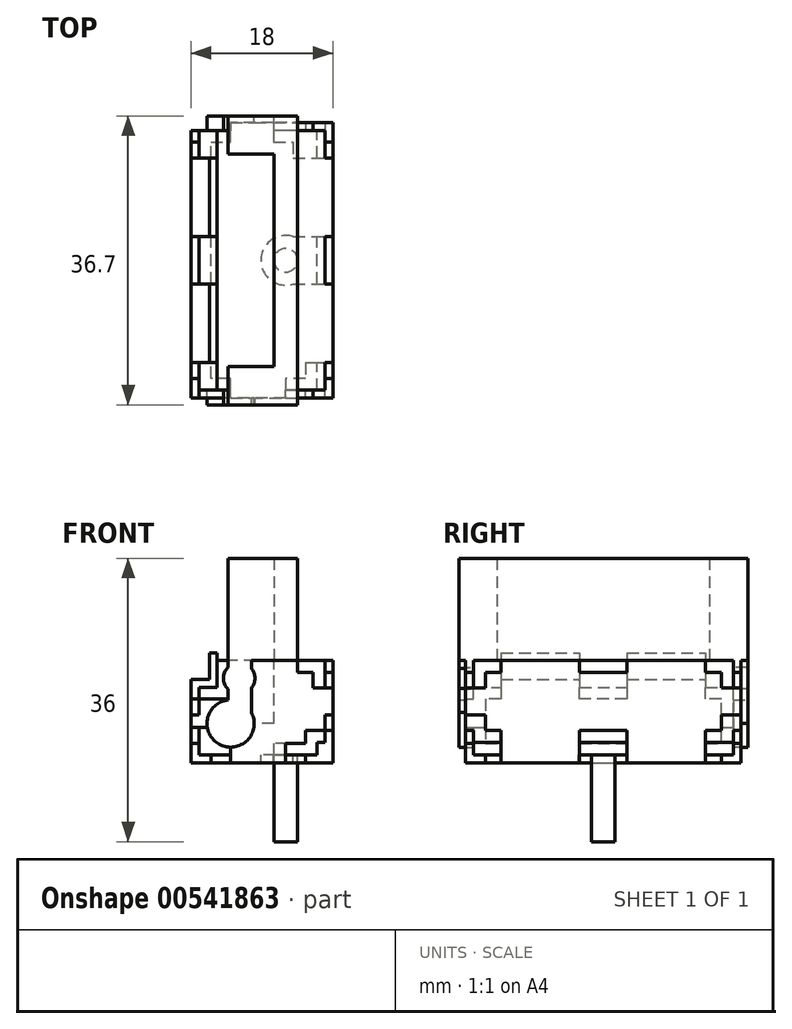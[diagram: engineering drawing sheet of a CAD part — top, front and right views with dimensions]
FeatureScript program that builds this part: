
annotation { "Feature Type Name" : "Feature", "Feature Type Description" : "" }
export const myFeature = defineFeature(function(context is Context, id is Id, definition is map)
    precondition{}
    {
        {
            var Q0;
            Q0=qCreatedBy(makeId("Front.planeOp"),FACE);
            var sketch = newSketch(context, id + "F0", { "sketchPlane" : qUnion([Q0])});
            skLineSegment(sketch, "E0", {"start": v(0, 0) * mm, "end": v(0, 8.6) * mm});
            skLineSegment(sketch, "E1", {"start": v(0, 8.6) * mm, "end": v(2.3, 8.6) * mm});
            skLineSegment(sketch, "E2", {"start": v(2.3, 8.6) * mm, "end": v(2.3, 12) * mm});
            skLineSegment(sketch, "E3", {"start": v(2.3, 12) * mm, "end": v(16, 12) * mm});
            skLineSegment(sketch, "E4", {"start": v(16, 12) * mm, "end": v(16, 1.6) * mm});
            skLineSegment(sketch, "E5", {"start": v(16, 1.6) * mm, "end": v(15, 1.6) * mm});
            skLineSegment(sketch, "E6", {"start": v(15, 1.6) * mm, "end": v(15, 0) * mm});
            skLineSegment(sketch, "E7", {"start": v(15, 0) * mm, "end": v(0, 0) * mm});
            skCircle(sketch, "E8", {"center": v(4, 4) * mm, "radius": 3 * mm});
            skCircle(sketch, "E9", {"center": v(5.1, 9.75) * mm, "radius": 2 * mm});
            skSolve(sketch);
        }
        {
            var Q0;
            Q0=makeQuery(id+"F0.imprint","IMPRINT",FACE,{"disambiguationData":[TD([[makeQuery(id+"F0.imprint","IMPRINT",EDGE,{"derivedFrom":sQuery(id+"F0.wireOp",EDGE,"E8")}),1.0]])]});
            var Q1;
            Q1=makeQuery(id+"F0.imprint","IMPRINT",FACE,{"disambiguationData":[TD([[makeQuery(id+"F0.imprint","IMPRINT",EDGE,{"derivedFrom":sQuery(id+"F0.wireOp",EDGE,"E9")}),1.0]])]});
            var Q2;
            Q2=makeQuery(id+"F0.imprint","IMPRINT",FACE,{"disambiguationData":[TD([[makeQuery(id+"F0.imprint","IMPRINT",EDGE,{"derivedFrom":sQuery(id+"F0.wireOp",EDGE,"E0")}),-1.0]])]});
            extrude(context, id + "F1", {"entities" : qUnion([Q0, Q1, Q2]), "depth" : 16.5 * mm, "offsetDistance" : 25 * mm, "hasSecondDirection" : true, "secondDirectionOppositeDirection" : true, "secondDirectionDepth" : 16.5 * mm});
        }
        {
            var Q0;
            Q0=makeQuery(id+"F1.opExtrude","SWEPT_FACE",FACE,{"disambiguationData":[OSD([sQuery(id+"F0.wireOp",EDGE,"E7")])]});
            var sketch = newSketch(context, id + "F2", { "sketchPlane" : qUnion([Q0])});
            skCircle(sketch, "E10", {"center": v(11, 0) * mm, "radius": 2.5 * mm});
            skCircle(sketch, "E11", {"center": v(11, 0) * mm, "radius": 1.5 * mm});
            skLineSegment(sketch, "E12", {"start": v(12.5, -18.35) * mm, "end": v(12.5, 18.35) * mm});
            skLineSegment(sketch, "E13", {"start": v(9.5, -18.35) * mm, "end": v(9.5, 18.35) * mm});
            skLineSegment(sketch, "E14", {"start": v(12.5, -18.35) * mm, "end": v(9.5, -18.35) * mm});
            skLineSegment(sketch, "E15", {"start": v(9.5, 18.35) * mm, "end": v(12.5, 18.35) * mm});
            skSolve(sketch);
        }
        {
            var Q0;
            Q0=makeQuery(id+"F0.imprint","IMPRINT",FACE,{"disambiguationData":[TD([[makeQuery(id+"F0.imprint","IMPRINT",EDGE,{"derivedFrom":sQuery(id+"F0.wireOp",EDGE,"E8")}),1.0]])]});
            extrude(context, id + "F3", {"entities" : qUnion([Q0]), "operationType" : NewBodyOperationType.ADD, "depth" : 36.7 * mm, "offsetDistance" : 25 * mm, "symmetric" : true});
        }
        {
            var Q0;
            Q0=makeQuery(id+"F2.imprint","IMPRINT",FACE,{"disambiguationData":[TD([[makeQuery(id+"F2.imprint","IMPRINT",EDGE,{"derivedFrom":sQuery(id+"F2.wireOp",EDGE,"E11")}),1.0]])]});
            var Q1;
            Q1=sQuery(id+"F2.wireOp",EDGE,"E11");
            extrude(context, id + "F4", {"entities" : qUnion([Q0]), "operationType" : NewBodyOperationType.ADD, "surfaceEntities" : qUnion([Q1]), "depth" : 11 * mm, "offsetDistance" : 25 * mm});
        }
        {
            var Q0;
            Q0=makeQuery(id+"F0.imprint","IMPRINT",FACE,{"disambiguationData":[TD([[makeQuery(id+"F0.imprint","IMPRINT",EDGE,{"derivedFrom":sQuery(id+"F0.wireOp",EDGE,"E9")}),1.0]])]});
            extrude(context, id + "F5", {"entities" : qUnion([Q0]), "operationType" : NewBodyOperationType.ADD, "depth" : 18.35 * mm, "offsetDistance" : 25 * mm});
        }
        {
            var Q0;
            Q0=makeQuery(id+"F0.imprint","IMPRINT",FACE,{"disambiguationData":[TD([[makeQuery(id+"F0.imprint","IMPRINT",EDGE,{"derivedFrom":sQuery(id+"F0.wireOp",EDGE,"E9")}),1.0]])]});
            extrude(context, id + "F6", {"entities" : qUnion([Q0]), "oppositeDirection" : true, "depth" : 18.35 * mm, "offsetDistance" : 25 * mm});
        }
        {
            var Q0;
            {var subQ0=sQuery(id+"F2.wireOp",EDGE,"E15");Q0=makeQuery(id+"F2.imprint","IMPRINT",FACE,{"disambiguationData":[TD([[makeQuery(id+"F2.imprint","IMPRINT",EDGE,{"derivedFrom":subQ0}),-1.0]])]});}
            var Q1;
            {var subQ0=sQuery(id+"F2.wireOp",EDGE,"E13");var subQ1=sQuery(id+"F2.wireOp",EDGE,"E10");var subQ2=makeQuery(id+"F2.imprint","INTERSECT",VERTEX,{"disambiguationData":[OD(0.0)],"derivedFrom":[subQ1,subQ0]});Q1=makeQuery(id+"F2.imprint","IMPRINT",FACE,{"disambiguationData":[TD([[makeQuery(id+"F2.imprint","IMPRINT",EDGE,{"disambiguationData":[TD([[subQ2,1.0]])],"derivedFrom":subQ1}),-1.0]])]});}
            var Q2;
            {var subQ0=sQuery(id+"F2.wireOp",EDGE,"E13");var subQ1=sQuery(id+"F2.wireOp",EDGE,"E10");var subQ2=makeQuery(id+"F2.imprint","INTERSECT",VERTEX,{"disambiguationData":[OD(0.0)],"derivedFrom":[subQ1,subQ0]});Q2=makeQuery(id+"F2.imprint","IMPRINT",FACE,{"disambiguationData":[TD([[makeQuery(id+"F2.imprint","IMPRINT",EDGE,{"disambiguationData":[TD([[subQ2,1.0]])],"derivedFrom":subQ1}),1.0]])]});}
            var Q3;
            {var subQ0=sQuery(id+"F2.wireOp",EDGE,"E11");var subQ1=makeQuery(id+"F2.imprint","INTERSECT",VERTEX,{"derivedFrom":[subQ0,sQuery(id+"F2.wireOp",EDGE,"E12")]});Q3=makeQuery(id+"F2.imprint","IMPRINT",FACE,{"disambiguationData":[TD([[makeQuery(id+"F2.imprint","IMPRINT",EDGE,{"disambiguationData":[TD([[subQ1,-1.0]])],"derivedFrom":subQ0}),1.0]])]});}
            var Q4;
            {var subQ0=sQuery(id+"F2.wireOp",EDGE,"E13");var subQ1=sQuery(id+"F2.wireOp",EDGE,"E10");var subQ2=makeQuery(id+"F2.imprint","INTERSECT",VERTEX,{"disambiguationData":[OD(1.0)],"derivedFrom":[subQ1,subQ0]});Q4=makeQuery(id+"F2.imprint","IMPRINT",FACE,{"disambiguationData":[TD([[makeQuery(id+"F2.imprint","IMPRINT",EDGE,{"disambiguationData":[TD([[subQ2,-1.0]])],"derivedFrom":subQ1}),1.0]])]});}
            var Q5;
            {var subQ0=sQuery(id+"F2.wireOp",EDGE,"E13");var subQ1=sQuery(id+"F2.wireOp",EDGE,"E10");var subQ2=makeQuery(id+"F2.imprint","INTERSECT",VERTEX,{"disambiguationData":[OD(1.0)],"derivedFrom":[subQ1,subQ0]});Q5=makeQuery(id+"F2.imprint","IMPRINT",FACE,{"disambiguationData":[TD([[makeQuery(id+"F2.imprint","IMPRINT",EDGE,{"disambiguationData":[TD([[subQ2,-1.0]])],"derivedFrom":subQ1}),-1.0]])]});}
            var Q6;
            {var subQ0=sQuery(id+"F2.wireOp",EDGE,"E14");Q6=makeQuery(id+"F2.imprint","IMPRINT",FACE,{"disambiguationData":[TD([[makeQuery(id+"F2.imprint","IMPRINT",EDGE,{"derivedFrom":subQ0}),-1.0]])]});}
            var Q7;
            Q7=makeQuery(id+"F1.opExtrude","SWEPT_FACE",FACE,{"disambiguationData":[OSD([sQuery(id+"F0.wireOp",EDGE,"E3")])]});
            var Q8;
            Q8=makeQuery(id+"F1.opExtrude","SWEPT_FACE",FACE,{"disambiguationData":[OSD([sQuery(id+"F0.wireOp",EDGE,"E3")])]});
            extrude(context, id + "F7", {"entities" : qUnion([Q0, Q1, Q2, Q3, Q4, Q5, Q6]), "operationType" : NewBodyOperationType.ADD, "oppositeDirection" : true, "depth" : 25 * mm, "endBoundEntityFace" : qUnion([Q7]), "offsetDistance" : 25 * mm, "hasSecondDirection" : true, "secondDirectionBound" : BoundingType.UP_TO_SURFACE, "secondDirectionOppositeDirection" : true, "secondDirectionDepth" : 18 * mm, "secondDirectionBoundEntityFace" : qUnion([Q8])});
        }
        {
            var Q0;
            Q0=makeQuery(id+"F1.opExtrude","SWEPT_FACE",FACE,{"disambiguationData":[OSD([sQuery(id+"F0.wireOp",EDGE,"E4")])]});
            var sketch = newSketch(context, id + "F8", { "sketchPlane" : qUnion([Q0])});
            skLineSegment(sketch, "E16", {"start": v(-13, 1.6) * mm, "end": v(-13, 3.1) * mm});
            skLineSegment(sketch, "E17", {"start": v(-13, 3.1) * mm, "end": v(-15, 3.1) * mm});
            skLineSegment(sketch, "E18", {"start": v(-15, 3.1) * mm, "end": v(-15, 5.1) * mm});
            skLineSegment(sketch, "E19", {"start": v(-15, 5.1) * mm, "end": v(-16.5, 5.1) * mm});
            skLineSegment(sketch, "E20", {"start": v(-16.5, 5.1) * mm, "end": v(-16.5, 8.5) * mm});
            skLineSegment(sketch, "E21", {"start": v(-16.5, 8.5) * mm, "end": v(-15, 8.5) * mm});
            skLineSegment(sketch, "E22", {"start": v(-15, 8.5) * mm, "end": v(-15, 10.5) * mm});
            skLineSegment(sketch, "E23", {"start": v(-15, 10.5) * mm, "end": v(-13, 10.5) * mm});
            skLineSegment(sketch, "E24", {"start": v(-13, 10.5) * mm, "end": v(-13, 12) * mm});
            skLineSegment(sketch, "E25", {"start": v(-13, 12) * mm, "end": v(-3, 12) * mm});
            skLineSegment(sketch, "E26", {"start": v(-3, 12) * mm, "end": v(-3, 10.5) * mm});
            skLineSegment(sketch, "E27", {"start": v(-3, 10.5) * mm, "end": v(3, 10.5) * mm});
            skLineSegment(sketch, "E28", {"start": v(3, 10.5) * mm, "end": v(3, 12) * mm});
            skLineSegment(sketch, "E29", {"start": v(3, 12) * mm, "end": v(13, 12) * mm});
            skLineSegment(sketch, "E30", {"start": v(13, 12) * mm, "end": v(13, 10.5) * mm});
            skLineSegment(sketch, "E31", {"start": v(13, 10.5) * mm, "end": v(15, 10.5) * mm});
            skLineSegment(sketch, "E32", {"start": v(15, 10.5) * mm, "end": v(15, 8.5) * mm});
            skLineSegment(sketch, "E33", {"start": v(15, 8.5) * mm, "end": v(16.5, 8.5) * mm});
            skLineSegment(sketch, "E34", {"start": v(16.5, 8.5) * mm, "end": v(16.5, 5.1) * mm});
            skLineSegment(sketch, "E35", {"start": v(16.5, 5.1) * mm, "end": v(15, 5.1) * mm});
            skLineSegment(sketch, "E36", {"start": v(15, 5.1) * mm, "end": v(15, 3.1) * mm});
            skLineSegment(sketch, "E37", {"start": v(15, 3.1) * mm, "end": v(13, 3.1) * mm});
            skLineSegment(sketch, "E38", {"start": v(13, 3.1) * mm, "end": v(13, 1.6) * mm});
            skLineSegment(sketch, "E39", {"start": v(13, 1.6) * mm, "end": v(3, 1.6) * mm});
            skLineSegment(sketch, "E40", {"start": v(3, 1.6) * mm, "end": v(3, 3.1) * mm});
            skLineSegment(sketch, "E41", {"start": v(3, 3.1) * mm, "end": v(-3, 3.1) * mm});
            skLineSegment(sketch, "E42", {"start": v(-3, 3.1) * mm, "end": v(-3, 1.6) * mm});
            skLineSegment(sketch, "E43", {"start": v(-3, 1.6) * mm, "end": v(-13, 1.6) * mm});
            skSolve(sketch);
        }
        {
            var Q0;
            Q0 = qSketchRegion(id + "F8", true);
            extrude(context, id + "F9", {"entities" : qUnion([Q0]), "operationType" : NewBodyOperationType.ADD, "depth" : 1 * mm, "offsetDistance" : 25 * mm});
        }
        {
            var Q0;
            Q0=makeQuery(id+"F1.opExtrude","SWEPT_FACE",FACE,{"disambiguationData":[OSD([sQuery(id+"F0.wireOp",EDGE,"E0")])]});
            var sketch = newSketch(context, id + "F10", { "sketchPlane" : qUnion([Q0])});
            skLineSegment(sketch, "E44", {"start": v(-13, 0) * mm, "end": v(-13, 1.5) * mm});
            skLineSegment(sketch, "E45", {"start": v(-13, 1.5) * mm, "end": v(-15, 1.5) * mm});
            skLineSegment(sketch, "E46", {"start": v(-15, 1.5) * mm, "end": v(-15, 3.5) * mm});
            skLineSegment(sketch, "E47", {"start": v(-15, 3.5) * mm, "end": v(-16.5, 3.5) * mm});
            skLineSegment(sketch, "E48", {"start": v(-16.5, 3.5) * mm, "end": v(-16.5, 5.1) * mm});
            skLineSegment(sketch, "E49", {"start": v(-16.5, 5.1) * mm, "end": v(-15, 5.1) * mm});
            skLineSegment(sketch, "E50", {"start": v(-15, 5.1) * mm, "end": v(-15, 7.1) * mm});
            skLineSegment(sketch, "E51", {"start": v(-15, 7.1) * mm, "end": v(-13, 7.1) * mm});
            skLineSegment(sketch, "E52", {"start": v(-13, 7.1) * mm, "end": v(-13, 8.6) * mm});
            skLineSegment(sketch, "E53", {"start": v(-13, 8.6) * mm, "end": v(-3, 8.6) * mm});
            skLineSegment(sketch, "E54", {"start": v(-3, 8.6) * mm, "end": v(-3, 7.1) * mm});
            skLineSegment(sketch, "E55", {"start": v(-3, 7.1) * mm, "end": v(3, 7.1) * mm});
            skLineSegment(sketch, "E56", {"start": v(3, 7.1) * mm, "end": v(3, 8.6) * mm});
            skLineSegment(sketch, "E57", {"start": v(3, 8.6) * mm, "end": v(13, 8.6) * mm});
            skLineSegment(sketch, "E58", {"start": v(13, 8.6) * mm, "end": v(13, 7.1) * mm});
            skLineSegment(sketch, "E59", {"start": v(13, 7.1) * mm, "end": v(15, 7.1) * mm});
            skLineSegment(sketch, "E60", {"start": v(15, 7.1) * mm, "end": v(15, 5.1) * mm});
            skLineSegment(sketch, "E61", {"start": v(15, 5.1) * mm, "end": v(16.5, 5.1) * mm});
            skLineSegment(sketch, "E62", {"start": v(16.5, 5.1) * mm, "end": v(16.5, 3.5) * mm});
            skLineSegment(sketch, "E63", {"start": v(16.5, 3.5) * mm, "end": v(15, 3.5) * mm});
            skLineSegment(sketch, "E64", {"start": v(15, 3.5) * mm, "end": v(15, 1.5) * mm});
            skLineSegment(sketch, "E65", {"start": v(15, 1.5) * mm, "end": v(13, 1.5) * mm});
            skLineSegment(sketch, "E66", {"start": v(13, 1.5) * mm, "end": v(13, 0) * mm});
            skLineSegment(sketch, "E67", {"start": v(13, 0) * mm, "end": v(3, 0) * mm});
            skLineSegment(sketch, "E68", {"start": v(3, 0) * mm, "end": v(3, 1.5) * mm});
            skLineSegment(sketch, "E69", {"start": v(3, 1.5) * mm, "end": v(-3, 1.5) * mm});
            skLineSegment(sketch, "E70", {"start": v(-3, 1.5) * mm, "end": v(-3, 0) * mm});
            skLineSegment(sketch, "E71", {"start": v(-3, 0) * mm, "end": v(-13, 0) * mm});
            skSolve(sketch);
        }
        {
            var Q0;
            Q0 = qSketchRegion(id + "F10", true);
            extrude(context, id + "F11", {"entities" : qUnion([Q0]), "operationType" : NewBodyOperationType.ADD, "depth" : 1 * mm, "offsetDistance" : 25 * mm});
        }
        {
            var Q0;
            {var subQ0=sQuery(id+"F0.wireOp",EDGE,"E2");var subQ1=sQuery(id+"F0.wireOp",EDGE,"E3");Q0=makeQuery(id+"F7.boolean.opBoolean","SPLIT",FACE,{"disambiguationData":[TD([makeQuery(id+"F1.opExtrude","SWEPT_FACE",FACE,{"disambiguationData":[OSD([subQ0])]})])],"derivedFrom":makeQuery(id+"F1.opExtrude","SWEPT_FACE",FACE,{"disambiguationData":[OSD([subQ1])]})});}
            var sketch = newSketch(context, id + "F12", { "sketchPlane" : qUnion([Q0])});
            skLineSegment(sketch, "E72", {"start": v(9.5, -16.5) * mm, "end": v(6.65, -16.5) * mm});
            skLineSegment(sketch, "E73", {"start": v(6.65, -16.5) * mm, "end": v(6.65, -18.35) * mm});
            skLineSegment(sketch, "E74", {"start": v(6.65, -18.35) * mm, "end": v(3.65, -18.35) * mm});
            skLineSegment(sketch, "E75", {"start": v(3.65, -18.35) * mm, "end": v(3.65, -13.5) * mm});
            skLineSegment(sketch, "E76", {"start": v(3.65, -13.5) * mm, "end": v(9.5, -13.5) * mm});
            skLineSegment(sketch, "E77", {"start": v(9.5, -13.5) * mm, "end": v(9.5, -16.5) * mm});
            skLineSegment(sketch, "E78", {"start": v(6.65, -18.35) * mm, "end": v(9.5, -18.35) * mm});
            skLineSegment(sketch, "E79", {"start": v(9.5, -18.35) * mm, "end": v(9.5, -16.5) * mm});
            skLineSegment(sketch, "E80.bottom", {"start": v(9.5, 13.5) * mm, "end": v(3.65, 13.5) * mm});
            skLineSegment(sketch, "E80.top", {"start": v(9.5, 18.35) * mm, "end": v(3.65, 18.35) * mm});
            skLineSegment(sketch, "E80.left", {"start": v(9.5, 13.5) * mm, "end": v(9.5, 18.35) * mm});
            skLineSegment(sketch, "E80.right", {"start": v(3.65, 13.5) * mm, "end": v(3.65, 18.35) * mm});
            skLineSegment(sketch, "E81.bottom", {"start": v(9.5, 18.35) * mm, "end": v(6.65, 18.35) * mm});
            skLineSegment(sketch, "E81.top", {"start": v(9.5, 16.5) * mm, "end": v(6.65, 16.5) * mm});
            skLineSegment(sketch, "E81.left", {"start": v(9.5, 18.35) * mm, "end": v(9.5, 16.5) * mm});
            skLineSegment(sketch, "E81.right", {"start": v(6.65, 18.35) * mm, "end": v(6.65, 16.5) * mm});
            skLineSegment(sketch, "E82", {"start": v(14, -15) * mm, "end": v(15, -15) * mm});
            skLineSegment(sketch, "E83", {"start": v(15, -15) * mm, "end": v(15, -13) * mm});
            skLineSegment(sketch, "E84", {"start": v(15, -13) * mm, "end": v(17, -13) * mm});
            skLineSegment(sketch, "E85", {"start": v(17, -13) * mm, "end": v(17, -3) * mm});
            skLineSegment(sketch, "E86", {"start": v(17, -3) * mm, "end": v(15, -3) * mm});
            skLineSegment(sketch, "E87", {"start": v(15, -3) * mm, "end": v(15, 3) * mm});
            skLineSegment(sketch, "E88", {"start": v(15, 3) * mm, "end": v(17, 3) * mm});
            skLineSegment(sketch, "E89", {"start": v(17, 3) * mm, "end": v(17, 13) * mm});
            skLineSegment(sketch, "E90", {"start": v(17, 13) * mm, "end": v(15, 13) * mm});
            skLineSegment(sketch, "E91", {"start": v(15, 13) * mm, "end": v(15, 15) * mm});
            skLineSegment(sketch, "E92", {"start": v(15, 15) * mm, "end": v(12.5, 15) * mm});
            skLineSegment(sketch, "E93", {"start": v(12.5, 15) * mm, "end": v(12.5, 13) * mm});
            skLineSegment(sketch, "E94", {"start": v(12.5, 13) * mm, "end": v(12.5, 13) * mm});
            skLineSegment(sketch, "E95", {"start": v(12.5, 13) * mm, "end": v(12.5, 3) * mm});
            skLineSegment(sketch, "E96", {"start": v(12.5, 3) * mm, "end": v(14, 3) * mm});
            skLineSegment(sketch, "E97", {"start": v(14, 3) * mm, "end": v(14, -3) * mm});
            skLineSegment(sketch, "E98", {"start": v(14, -3) * mm, "end": v(12.5, -3) * mm});
            skLineSegment(sketch, "E99", {"start": v(12.5, -3) * mm, "end": v(12.5, -13) * mm});
            skLineSegment(sketch, "E100", {"start": v(12.5, -13) * mm, "end": v(14, -13) * mm});
            skLineSegment(sketch, "E101", {"start": v(14, -13) * mm, "end": v(14, -15) * mm});
            skLineSegment(sketch, "E102", {"start": v(3.8, -15) * mm, "end": v(8, -15) * mm});
            skLineSegment(sketch, "E103", {"start": v(3.8, -15) * mm, "end": v(3.8, -13) * mm});
            skLineSegment(sketch, "E104", {"start": v(2.3, -13) * mm, "end": v(3.8, -13) * mm});
            skLineSegment(sketch, "E105", {"start": v(2.3, -13) * mm, "end": v(2.3, -3) * mm});
            skLineSegment(sketch, "E106", {"start": v(3.8, -3) * mm, "end": v(2.3, -3) * mm});
            skLineSegment(sketch, "E107", {"start": v(3.8, -3) * mm, "end": v(3.8, 3) * mm});
            skLineSegment(sketch, "E108", {"start": v(2.3, 3) * mm, "end": v(3.8, 3) * mm});
            skLineSegment(sketch, "E109", {"start": v(2.3, 3) * mm, "end": v(2.3, 13) * mm});
            skLineSegment(sketch, "E110", {"start": v(3.8, 13) * mm, "end": v(2.3, 13) * mm});
            skLineSegment(sketch, "E111", {"start": v(3.8, 13) * mm, "end": v(3.8, 15) * mm});
            skLineSegment(sketch, "E112", {"start": v(8, 15) * mm, "end": v(3.8, 15) * mm});
            skLineSegment(sketch, "E113", {"start": v(8, 15) * mm, "end": v(8, 13) * mm});
            skLineSegment(sketch, "E114", {"start": v(9.5, 13) * mm, "end": v(8, 13) * mm});
            skLineSegment(sketch, "E115", {"start": v(9.5, 13) * mm, "end": v(9.5, 3) * mm});
            skLineSegment(sketch, "E116", {"start": v(8, 3) * mm, "end": v(9.5, 3) * mm});
            skLineSegment(sketch, "E117", {"start": v(8, 3) * mm, "end": v(8, -3) * mm});
            skLineSegment(sketch, "E118", {"start": v(9.5, -3) * mm, "end": v(8, -3) * mm});
            skLineSegment(sketch, "E119", {"start": v(9.5, -3) * mm, "end": v(9.5, -13) * mm});
            skLineSegment(sketch, "E120", {"start": v(8, -13) * mm, "end": v(9.5, -13) * mm});
            skLineSegment(sketch, "E121", {"start": v(8, -13) * mm, "end": v(8, -15) * mm});
            skSolve(sketch);
        }
        {
            var Q0;
            {var subQ0=sQuery(id+"F12.wireOp",EDGE,"E73");Q0=makeQuery(id+"F12.imprint","IMPRINT",FACE,{"disambiguationData":[TD([[makeQuery(id+"F12.imprint","IMPRINT",EDGE,{"derivedFrom":subQ0}),-1.0]])]});}
            var Q1;
            {var subQ8=sQuery(id+"F12.wireOp",EDGE,"E72");Q1=makeQuery(id+"F12.imprint","IMPRINT",FACE,{"disambiguationData":[TD([[makeQuery(id+"F12.imprint","IMPRINT",EDGE,{"derivedFrom":subQ8}),1.0]])]});}
            var Q2;
            Q2=makeQuery(id+"F12.imprint","IMPRINT",FACE,{"disambiguationData":[TD([[makeQuery(id+"F12.imprint","IMPRINT",EDGE,{"derivedFrom":sQuery(id+"F12.wireOp",EDGE,"E72")}),-1.0]])]});
            var Q3;
            {var subQ5=sQuery(id+"F12.wireOp",EDGE,"E102");Q3=makeQuery(id+"F12.imprint","IMPRINT",FACE,{"disambiguationData":[TD([[makeQuery(id+"F12.imprint","IMPRINT",EDGE,{"derivedFrom":subQ5}),1.0]])]});}
            var Q4;
            Q4=makeQuery(id+"F7.opExtrude","CAP_FACE",FACE,{"disambiguationData":[OSD([sQuery(id+"F2.wireOp",EDGE,"E12"),sQuery(id+"F2.wireOp",EDGE,"E13"),sQuery(id+"F2.wireOp",EDGE,"E14"),sQuery(id+"F2.wireOp",EDGE,"E15")])],"isStart":false});
            extrude(context, id + "F13", {"entities" : qUnion([Q0, Q1, Q2, Q3]), "operationType" : NewBodyOperationType.ADD, "endBound" : BoundingType.UP_TO_SURFACE, "depth" : 25 * mm, "endBoundEntityFace" : qUnion([Q4]), "offsetDistance" : 25 * mm});
        }
        {
            var Q0;
            Q0=makeQuery(id+"F12.imprint","IMPRINT",FACE,{"disambiguationData":[TD([[makeQuery(id+"F12.imprint","IMPRINT",EDGE,{"derivedFrom":sQuery(id+"F12.wireOp",EDGE,"E81.bottom")}),1.0]])]});
            var Q1;
            {var subQ0=sQuery(id+"F12.wireOp",EDGE,"E80.top");Q1=makeQuery(id+"F12.imprint","IMPRINT",FACE,{"disambiguationData":[TD([[makeQuery(id+"F12.imprint","IMPRINT",EDGE,{"derivedFrom":subQ0}),1.0]])]});}
            var Q2;
            {var subQ0=sQuery(id+"F12.wireOp",EDGE,"E80.left");Q2=makeQuery(id+"F12.imprint","IMPRINT",FACE,{"disambiguationData":[TD([[makeQuery(id+"F12.imprint","IMPRINT",EDGE,{"derivedFrom":subQ0}),-1.0]])]});}
            var Q3;
            {var subQ5=sQuery(id+"F12.wireOp",EDGE,"E112");Q3=makeQuery(id+"F12.imprint","IMPRINT",FACE,{"disambiguationData":[TD([[makeQuery(id+"F12.imprint","IMPRINT",EDGE,{"derivedFrom":subQ5}),1.0]])]});}
            var Q4;
            {var subQ0=sQuery(id+"F2.wireOp",EDGE,"E15");var subQ1=sQuery(id+"F2.wireOp",EDGE,"E14");var subQ2=sQuery(id+"F2.wireOp",EDGE,"E13");var subQ3=sQuery(id+"F2.wireOp",EDGE,"E12");Q4=makeQuery(id+"F13.boolean.opBoolean","MERGE",FACE,{"derivedFrom":[makeQuery(id+"F7.opExtrude","CAP_FACE",FACE,{"disambiguationData":[OSD([subQ3,subQ2,subQ1,subQ0])],"isStart":false}),makeQuery(id+"F13.opExtrude","CAP_FACE",FACE,{"disambiguationData":[OSD([subQ3,subQ2,subQ1,subQ0])],"isStart":false})]});}
            extrude(context, id + "F14", {"entities" : qUnion([Q0, Q1, Q2, Q3]), "operationType" : NewBodyOperationType.ADD, "endBound" : BoundingType.UP_TO_SURFACE, "depth" : 25 * mm, "endBoundEntityFace" : qUnion([Q4]), "offsetDistance" : 25 * mm});
        }
        {
            var Q0;
            {var subQ0=sQuery(id+"F12.wireOp",EDGE,"E73");Q0=makeQuery(id+"F12.imprint","IMPRINT",FACE,{"disambiguationData":[TD([[makeQuery(id+"F12.imprint","IMPRINT",EDGE,{"derivedFrom":subQ0}),-1.0]])]});}
            extrude(context, id + "F15", {"entities" : qUnion([Q0]), "operationType" : NewBodyOperationType.ADD, "oppositeDirection" : true, "depth" : 8 * mm, "offsetDistance" : 25 * mm});
        }
        {
            var Q0;
            {var subQ0=sQuery(id+"F12.wireOp",EDGE,"E80.top");Q0=makeQuery(id+"F12.imprint","IMPRINT",FACE,{"disambiguationData":[TD([[makeQuery(id+"F12.imprint","IMPRINT",EDGE,{"derivedFrom":subQ0}),1.0]])]});}
            extrude(context, id + "F16", {"entities" : qUnion([Q0]), "operationType" : NewBodyOperationType.ADD, "oppositeDirection" : true, "depth" : 8 * mm, "offsetDistance" : 25 * mm});
        }
        {
            var Q0;
            Q0=makeQuery(id+"F11.boolean.opBoolean","MERGE",FACE,{"derivedFrom":[makeQuery(id+"F1.opExtrude","SWEPT_FACE",FACE,{"disambiguationData":[OSD([sQuery(id+"F0.wireOp",EDGE,"E1")])]}),makeQuery(id+"F11.opExtrude","SWEPT_FACE",FACE,{"disambiguationData":[OSD([sQuery(id+"F10.wireOp",EDGE,"E53")])]}),makeQuery(id+"F11.opExtrude","SWEPT_FACE",FACE,{"disambiguationData":[OSD([sQuery(id+"F10.wireOp",EDGE,"E57")])]})]});
            var sketch = newSketch(context, id + "F17", { "sketchPlane" : qUnion([Q0])});
            skLineSegment(sketch, "E122.bottom", {"start": v(-1, -13) * mm, "end": v(2.3, -13) * mm});
            skLineSegment(sketch, "E122.top", {"start": v(-1, -3) * mm, "end": v(2.3, -3) * mm});
            skLineSegment(sketch, "E122.left", {"start": v(-1, -13) * mm, "end": v(-1, -3) * mm});
            skLineSegment(sketch, "E122.right", {"start": v(2.3, -13) * mm, "end": v(2.3, -3) * mm});
            skLineSegment(sketch, "E123.bottom", {"start": v(-1, 3) * mm, "end": v(2.3, 3) * mm});
            skLineSegment(sketch, "E123.top", {"start": v(-1, 13) * mm, "end": v(2.3, 13) * mm});
            skLineSegment(sketch, "E123.left", {"start": v(-1, 3) * mm, "end": v(-1, 13) * mm});
            skLineSegment(sketch, "E123.right", {"start": v(2.3, 3) * mm, "end": v(2.3, 13) * mm});
            skSolve(sketch);
        }
        {
            var Q0;
            Q0 = qSketchRegion(id + "F17", true);
            extrude(context, id + "F18", {"entities" : qUnion([Q0]), "operationType" : NewBodyOperationType.ADD, "depth" : 1 * mm, "offsetDistance" : 25 * mm});
        }
        {
            var Q0;
            Q0=makeQuery(id+"Frkbs0kmV5nEgZC_1.boolean.opBoolean","MERGE",FACE,{"derivedFrom":[makeQuery(id+"F1.opExtrude","SWEPT_FACE",FACE,{"disambiguationData":[OSD([sQuery(id+"F0.wireOp",EDGE,"E2")])]}),makeQuery(id+"Frkbs0kmV5nEgZC_1.opExtrude","SWEPT_FACE",FACE,{"disambiguationData":[OSD([sQuery(id+"F12.wireOp",EDGE,"E105")])]}),makeQuery(id+"Frkbs0kmV5nEgZC_1.opExtrude","SWEPT_FACE",FACE,{"disambiguationData":[OSD([sQuery(id+"F12.wireOp",EDGE,"E109")])]})]});
            var sketch = newSketch(context, id + "F19", { "sketchPlane" : qUnion([Q0])});
            skLineSegment(sketch, "E124.bottom", {"start": v(13, 8.6) * mm, "end": v(3, 8.6) * mm});
            skLineSegment(sketch, "E124.top", {"start": v(13, 13) * mm, "end": v(3, 13) * mm});
            skLineSegment(sketch, "E124.left", {"start": v(13, 8.6) * mm, "end": v(13, 13) * mm});
            skLineSegment(sketch, "E124.right", {"start": v(3, 8.6) * mm, "end": v(3, 13) * mm});
            skLineSegment(sketch, "E125.bottom", {"start": v(-3, 8.6) * mm, "end": v(-13, 8.6) * mm});
            skLineSegment(sketch, "E125.top", {"start": v(-3, 13) * mm, "end": v(-13, 13) * mm});
            skLineSegment(sketch, "E125.left", {"start": v(-3, 8.6) * mm, "end": v(-3, 13) * mm});
            skLineSegment(sketch, "E125.right", {"start": v(-13, 8.6) * mm, "end": v(-13, 13) * mm});
            skSolve(sketch);
        }
        {
            var Q0;
            Q0 = qSketchRegion(id + "F19", true);
            extrude(context, id + "F20", {"entities" : qUnion([Q0]), "operationType" : NewBodyOperationType.ADD, "depth" : 1 * mm, "offsetDistance" : 25 * mm});
        }
        {
            var Q0;
            Q0=makeQuery(id+"F9.boolean.opBoolean","MERGE",FACE,{"derivedFrom":[makeQuery(id+"F1.opExtrude","SWEPT_FACE",FACE,{"disambiguationData":[OSD([sQuery(id+"F0.wireOp",EDGE,"E5")])]}),makeQuery(id+"F9.opExtrude","SWEPT_FACE",FACE,{"disambiguationData":[OSD([sQuery(id+"F8.wireOp",EDGE,"E39")])]}),makeQuery(id+"F9.opExtrude","SWEPT_FACE",FACE,{"disambiguationData":[OSD([sQuery(id+"F8.wireOp",EDGE,"E43")])]})]});
            var sketch = newSketch(context, id + "F21", { "sketchPlane" : qUnion([Q0])});
            skLineSegment(sketch, "E126.bottom", {"start": v(15, 13) * mm, "end": v(17, 13) * mm});
            skLineSegment(sketch, "E126.top", {"start": v(15, 3) * mm, "end": v(17, 3) * mm});
            skLineSegment(sketch, "E126.left", {"start": v(15, 13) * mm, "end": v(15, 3) * mm});
            skLineSegment(sketch, "E126.right", {"start": v(17, 13) * mm, "end": v(17, 3) * mm});
            skLineSegment(sketch, "E127.bottom", {"start": v(15, -3) * mm, "end": v(17, -3) * mm});
            skLineSegment(sketch, "E127.top", {"start": v(15, -13) * mm, "end": v(17, -13) * mm});
            skLineSegment(sketch, "E127.left", {"start": v(15, -3) * mm, "end": v(15, -13) * mm});
            skLineSegment(sketch, "E127.right", {"start": v(17, -3) * mm, "end": v(17, -13) * mm});
            skSolve(sketch);
        }
        {
            var Q0;
            {var subQ10=sQuery(id+"F21.wireOp",EDGE,"E126.left");Q0=makeQuery(id+"F21.imprint","IMPRINT",FACE,{"disambiguationData":[TD([[makeQuery(id+"F21.imprint","IMPRINT",EDGE,{"derivedFrom":subQ10}),1.0]])]});}
            var Q1;
            {var subQ11=sQuery(id+"F21.wireOp",EDGE,"E127.left");Q1=makeQuery(id+"F21.imprint","IMPRINT",FACE,{"disambiguationData":[TD([[makeQuery(id+"F21.imprint","IMPRINT",EDGE,{"derivedFrom":subQ11}),1.0]])]});}
            var Q2;
            Q2=makeQuery(id+"F11.boolean.opBoolean","MERGE",FACE,{"derivedFrom":[makeQuery(id+"F1.opExtrude","SWEPT_FACE",FACE,{"disambiguationData":[OSD([sQuery(id+"F0.wireOp",EDGE,"E7")])]}),makeQuery(id+"F11.opExtrude","SWEPT_FACE",FACE,{"disambiguationData":[OSD([sQuery(id+"F10.wireOp",EDGE,"E67")])]}),makeQuery(id+"F11.opExtrude","SWEPT_FACE",FACE,{"disambiguationData":[OSD([sQuery(id+"F10.wireOp",EDGE,"E71")])]})]});
            extrude(context, id + "F22", {"entities" : qUnion([Q0, Q1]), "operationType" : NewBodyOperationType.ADD, "endBound" : BoundingType.UP_TO_SURFACE, "depth" : 2 * mm, "endBoundEntityFace" : qUnion([Q2]), "offsetDistance" : 25 * mm});
        }
        {
            var Q0;
            {var subQ0=sQuery(id+"F10.wireOp",EDGE,"E71");var subQ1=sQuery(id+"F10.wireOp",EDGE,"E67");var subQ2=sQuery(id+"F0.wireOp",EDGE,"E7");Q0=makeQuery(id+"F22.boolean.opBoolean","MERGE",FACE,{"derivedFrom":[makeQuery(id+"F11.boolean.opBoolean","MERGE",FACE,{"derivedFrom":[makeQuery(id+"F1.opExtrude","SWEPT_FACE",FACE,{"disambiguationData":[OSD([subQ2])]}),makeQuery(id+"F11.opExtrude","SWEPT_FACE",FACE,{"disambiguationData":[OSD([subQ1])]}),makeQuery(id+"F11.opExtrude","SWEPT_FACE",FACE,{"disambiguationData":[OSD([subQ0])]})]}),makeQuery(id+"F22.opExtrude","CAP_FACE",FACE,{"disambiguationData":[OSD([subQ2,subQ1,subQ0]),OD(0.0)],"isStart":false}),makeQuery(id+"F22.opExtrude","CAP_FACE",FACE,{"disambiguationData":[OSD([subQ2,subQ1,subQ0]),OD(1.0)],"isStart":false})]});}
            var sketch = newSketch(context, id + "F23", { "sketchPlane" : qUnion([Q0])});
            skLineSegment(sketch, "E128", {"start": v(17, -13) * mm, "end": v(17, -3) * mm});
            skLineSegment(sketch, "E129", {"start": v(17, -3) * mm, "end": v(11.96, -3) * mm});
            skLineSegment(sketch, "E130", {"start": v(11.96, -3) * mm, "end": v(11.96, 3) * mm});
            skLineSegment(sketch, "E131", {"start": v(11.96, 3) * mm, "end": v(17, 3) * mm});
            skLineSegment(sketch, "E132", {"start": v(17, 3) * mm, "end": v(17, 13) * mm});
            skLineSegment(sketch, "E133", {"start": v(17, 13) * mm, "end": v(13.5, 13) * mm});
            skLineSegment(sketch, "E134", {"start": v(13.5, 13) * mm, "end": v(13.5, 15) * mm});
            skLineSegment(sketch, "E135", {"start": v(13.5, 15) * mm, "end": v(11, 15) * mm});
            skLineSegment(sketch, "E136", {"start": v(11, 15) * mm, "end": v(11, 16.5) * mm});
            skLineSegment(sketch, "E137", {"start": v(11, 16.5) * mm, "end": v(4, 16.5) * mm});
            skLineSegment(sketch, "E138", {"start": v(4, 16.5) * mm, "end": v(4, 15) * mm});
            skLineSegment(sketch, "E139", {"start": v(4, 15) * mm, "end": v(1.5, 15) * mm});
            skLineSegment(sketch, "E140", {"start": v(1.5, 15) * mm, "end": v(1.5, 13) * mm});
            skLineSegment(sketch, "E141", {"start": v(1.5, 13) * mm, "end": v(-1, 13) * mm});
            skLineSegment(sketch, "E142", {"start": v(-1, 13) * mm, "end": v(-1, 3) * mm});
            skLineSegment(sketch, "E143", {"start": v(-1, 3) * mm, "end": v(1.5, 3) * mm});
            skLineSegment(sketch, "E144", {"start": v(1.5, 3) * mm, "end": v(1.5, -3) * mm});
            skLineSegment(sketch, "E145", {"start": v(1.5, -3) * mm, "end": v(-1, -3) * mm});
            skLineSegment(sketch, "E146", {"start": v(-1, -3) * mm, "end": v(-1, -13) * mm});
            skLineSegment(sketch, "E147", {"start": v(-1, -13) * mm, "end": v(1.5, -13) * mm});
            skLineSegment(sketch, "E148", {"start": v(1.5, -13) * mm, "end": v(1.5, -15) * mm});
            skLineSegment(sketch, "E149", {"start": v(1.5, -15) * mm, "end": v(4, -15) * mm});
            skLineSegment(sketch, "E150", {"start": v(4, -15) * mm, "end": v(4, -16.5) * mm});
            skLineSegment(sketch, "E151", {"start": v(4, -16.5) * mm, "end": v(9.46, -16.5) * mm});
            skLineSegment(sketch, "E152", {"start": v(9.46, -16.5) * mm, "end": v(9.46, -15) * mm});
            skLineSegment(sketch, "E153", {"start": v(9.46, -15) * mm, "end": v(11.96, -15) * mm});
            skLineSegment(sketch, "E154", {"start": v(11.96, -15) * mm, "end": v(11.96, -13) * mm});
            skLineSegment(sketch, "E155", {"start": v(11.96, -13) * mm, "end": v(17, -13) * mm});
            skCircle(sketch, "E156", {"center": v(11, 0) * mm, "radius": 3.15 * mm});
            skSolve(sketch);
        }
        {
            var Q0;
            {var subQ41=sQuery(id+"F23.wireOp",EDGE,"E128");Q0=makeQuery(id+"F23.imprint","IMPRINT",FACE,{"disambiguationData":[TD([[makeQuery(id+"F23.imprint","IMPRINT",EDGE,{"derivedFrom":subQ41}),-1.0]])]});}
            var Q1;
            {var subQ0=sQuery(id+"F23.wireOp",EDGE,"E130");var subQ1=makeQuery(id+"F4.opExtrude","CAP_EDGE",EDGE,{"disambiguationData":[OSD([sQuery(id+"F2.wireOp",EDGE,"E11")])],"isStart":true});var subQ2=makeQuery(id+"F23.imprint","INTERSECT",VERTEX,{"disambiguationData":[OD(0.0)],"derivedFrom":[subQ1,subQ0]});Q1=makeQuery(id+"F23.imprint","IMPRINT",FACE,{"disambiguationData":[TD([[makeQuery(id+"F23.imprint","IMPRINT",EDGE,{"disambiguationData":[TD([[subQ2,-1.0]])],"derivedFrom":subQ0}),1.0]])]});}
            var Q2;
            {var subQ0=sQuery(id+"F23.wireOp",EDGE,"E130");var subQ1=makeQuery(id+"F4.opExtrude","CAP_EDGE",EDGE,{"disambiguationData":[OSD([sQuery(id+"F2.wireOp",EDGE,"E11")])],"isStart":true});var subQ2=makeQuery(id+"F23.imprint","INTERSECT",VERTEX,{"disambiguationData":[OD(0.0)],"derivedFrom":[subQ1,subQ0]});Q2=makeQuery(id+"F23.imprint","IMPRINT",FACE,{"disambiguationData":[TD([[makeQuery(id+"F23.imprint","IMPRINT",EDGE,{"disambiguationData":[TD([[subQ2,-1.0]])],"derivedFrom":subQ0}),-1.0]])]});}
            extrude(context, id + "F24", {"entities" : qUnion([Q0, Q1, Q2]), "operationType" : NewBodyOperationType.ADD, "depth" : 1 * mm, "offsetDistance" : 25 * mm});
        }
        {
            var Q0;
            Q0=makeQuery(id+"F24.boolean.opBoolean","MERGE",FACE,{"derivedFrom":[makeQuery(id+"F11.boolean.opBoolean","MERGE",FACE,{"derivedFrom":[makeQuery(id+"F9.boolean.opBoolean","MERGE",FACE,{"derivedFrom":[makeQuery(id+"F1.opExtrude","CAP_FACE",FACE,{"disambiguationData":[OSD([sQuery(id+"F0.wireOp",EDGE,"E0"),sQuery(id+"F0.wireOp",EDGE,"E1"),sQuery(id+"F0.wireOp",EDGE,"E2"),sQuery(id+"F0.wireOp",EDGE,"E3"),sQuery(id+"F0.wireOp",EDGE,"E4"),sQuery(id+"F0.wireOp",EDGE,"E5"),sQuery(id+"F0.wireOp",EDGE,"E6"),sQuery(id+"F0.wireOp",EDGE,"E7")])],"isStart":true}),makeQuery(id+"F9.opExtrude","SWEPT_FACE",FACE,{"disambiguationData":[OSD([sQuery(id+"F8.wireOp",EDGE,"E34")])]})]}),makeQuery(id+"F11.opExtrude","SWEPT_FACE",FACE,{"disambiguationData":[OSD([sQuery(id+"F10.wireOp",EDGE,"E48")])]})]}),makeQuery(id+"F24.opExtrude","SWEPT_FACE",FACE,{"disambiguationData":[OSD([sQuery(id+"F23.wireOp",EDGE,"E151")])]})]});
            var sketch = newSketch(context, id + "F25", { "sketchPlane" : qUnion([Q0])});
            skLineSegment(sketch, "E157", {"start": v(-14.5, 10.5) * mm, "end": v(-14.5, 8.5) * mm});
            skLineSegment(sketch, "E158", {"start": v(-14.5, 8.5) * mm, "end": v(-17, 8.5) * mm});
            skLineSegment(sketch, "E159", {"start": v(-17, 8.5) * mm, "end": v(-17, 5.1) * mm});
            skLineSegment(sketch, "E160", {"start": v(-17, 5.1) * mm, "end": v(-16, 5.1) * mm});
            skLineSegment(sketch, "E161", {"start": v(-16, 5.1) * mm, "end": v(-16, 3.1) * mm});
            skLineSegment(sketch, "E162", {"start": v(-16, 3.1) * mm, "end": v(-13.5, 3.1) * mm});
            skLineSegment(sketch, "E163", {"start": v(-13.5, 3.1) * mm, "end": v(-13.5, 1.5) * mm});
            skLineSegment(sketch, "E164", {"start": v(-13.5, 1.5) * mm, "end": v(-9.46, 1.5) * mm});
            skLineSegment(sketch, "E165", {"start": v(-9.46, 1.5) * mm, "end": v(-9.46, -1) * mm});
            skLineSegment(sketch, "E166", {"start": v(-9.46, -1) * mm, "end": v(-4, -1) * mm});
            skLineSegment(sketch, "E167", {"start": v(-4, -1) * mm, "end": v(-4, 1.5) * mm});
            skLineSegment(sketch, "E168", {"start": v(-4, 1.5) * mm, "end": v(-1.5, 1.5) * mm});
            skLineSegment(sketch, "E169", {"start": v(-1.5, 1.5) * mm, "end": v(-1.5, 3.5) * mm});
            skLineSegment(sketch, "E170", {"start": v(-1.5, 3.5) * mm, "end": v(1, 3.5) * mm});
            skLineSegment(sketch, "E171", {"start": v(1, 3.5) * mm, "end": v(1, 5.1) * mm});
            skLineSegment(sketch, "E172", {"start": v(1, 5.1) * mm, "end": v(0, 5.1) * mm});
            skLineSegment(sketch, "E173", {"start": v(0, 5.1) * mm, "end": v(0, 7.1) * mm});
            skLineSegment(sketch, "E174", {"start": v(0, 7.1) * mm, "end": v(-3.65, 7.1) * mm});
            skLineSegment(sketch, "E175", {"start": v(-3.65, 7.1) * mm, "end": v(-3.65, 12) * mm});
            skLineSegment(sketch, "E176", {"start": v(-3.65, 12) * mm, "end": v(-12.5, 12) * mm});
            skLineSegment(sketch, "E177", {"start": v(-12.5, 12) * mm, "end": v(-12.5, 10.5) * mm});
            skLineSegment(sketch, "E178", {"start": v(-12.5, 10.5) * mm, "end": v(-14.5, 10.5) * mm});
            skSolve(sketch);
        }
        {
            var Q0;
            {var subQ36=sQuery(id+"F25.wireOp",EDGE,"E157");Q0=makeQuery(id+"F25.imprint","IMPRINT",FACE,{"disambiguationData":[TD([[makeQuery(id+"F25.imprint","IMPRINT",EDGE,{"derivedFrom":subQ36}),1.0]])]});}
            extrude(context, id + "F26", {"entities" : qUnion([Q0]), "operationType" : NewBodyOperationType.ADD, "depth" : 1 * mm, "offsetDistance" : 25 * mm});
        }
        {
            var Q0;
            Q0=makeQuery(id+"F24.boolean.opBoolean","MERGE",FACE,{"derivedFrom":[makeQuery(id+"F11.boolean.opBoolean","MERGE",FACE,{"derivedFrom":[makeQuery(id+"F9.boolean.opBoolean","MERGE",FACE,{"derivedFrom":[makeQuery(id+"F1.opExtrude","CAP_FACE",FACE,{"disambiguationData":[OSD([sQuery(id+"F0.wireOp",EDGE,"E0"),sQuery(id+"F0.wireOp",EDGE,"E1"),sQuery(id+"F0.wireOp",EDGE,"E2"),sQuery(id+"F0.wireOp",EDGE,"E3"),sQuery(id+"F0.wireOp",EDGE,"E4"),sQuery(id+"F0.wireOp",EDGE,"E5"),sQuery(id+"F0.wireOp",EDGE,"E6"),sQuery(id+"F0.wireOp",EDGE,"E7")])],"isStart":false}),makeQuery(id+"F9.opExtrude","SWEPT_FACE",FACE,{"disambiguationData":[OSD([sQuery(id+"F8.wireOp",EDGE,"E20")])]})]}),makeQuery(id+"F11.opExtrude","SWEPT_FACE",FACE,{"disambiguationData":[OSD([sQuery(id+"F10.wireOp",EDGE,"E62")])]})]}),makeQuery(id+"F24.opExtrude","SWEPT_FACE",FACE,{"disambiguationData":[OSD([sQuery(id+"F23.wireOp",EDGE,"E137")])]})]});
            var sketch = newSketch(context, id + "F27", { "sketchPlane" : qUnion([Q0])});
            skLineSegment(sketch, "E179", {"start": v(4, -1) * mm, "end": v(11, -1) * mm});
            skLineSegment(sketch, "E180", {"start": v(11, -1) * mm, "end": v(11, 1.5) * mm});
            skLineSegment(sketch, "E181", {"start": v(11, 1.5) * mm, "end": v(13.5, 1.5) * mm});
            skLineSegment(sketch, "E182", {"start": v(13.5, 1.5) * mm, "end": v(13.5, 3.1) * mm});
            skLineSegment(sketch, "E183", {"start": v(13.5, 3.1) * mm, "end": v(16, 3.1) * mm});
            skLineSegment(sketch, "E184", {"start": v(16, 3.1) * mm, "end": v(16, 5.1) * mm});
            skLineSegment(sketch, "E185", {"start": v(16, 5.1) * mm, "end": v(17, 5.1) * mm});
            skLineSegment(sketch, "E186", {"start": v(17, 5.1) * mm, "end": v(17, 8.5) * mm});
            skLineSegment(sketch, "E187", {"start": v(17, 8.5) * mm, "end": v(16, 8.5) * mm});
            skLineSegment(sketch, "E188", {"start": v(16, 8.5) * mm, "end": v(14.5, 8.5) * mm});
            skLineSegment(sketch, "E189", {"start": v(14.5, 8.5) * mm, "end": v(14.5, 10.5) * mm});
            skLineSegment(sketch, "E190", {"start": v(14.5, 10.5) * mm, "end": v(12.5, 10.5) * mm});
            skLineSegment(sketch, "E191", {"start": v(12.5, 10.5) * mm, "end": v(12.5, 12) * mm});
            skLineSegment(sketch, "E192", {"start": v(12.5, 12) * mm, "end": v(3.65, 12) * mm});
            skLineSegment(sketch, "E193", {"start": v(3.65, 12) * mm, "end": v(3.65, 7.1) * mm});
            skLineSegment(sketch, "E194", {"start": v(3.65, 7.1) * mm, "end": v(0, 7.1) * mm});
            skLineSegment(sketch, "E195", {"start": v(0, 7.1) * mm, "end": v(0, 5.1) * mm});
            skLineSegment(sketch, "E196", {"start": v(0, 5.1) * mm, "end": v(-1, 5.1) * mm});
            skLineSegment(sketch, "E197", {"start": v(-1, 5.1) * mm, "end": v(-1, 3.5) * mm});
            skLineSegment(sketch, "E198", {"start": v(-1, 3.5) * mm, "end": v(0, 3.5) * mm});
            skLineSegment(sketch, "E199", {"start": v(0, 3.5) * mm, "end": v(1.5, 3.5) * mm});
            skLineSegment(sketch, "E200", {"start": v(1.5, 3.5) * mm, "end": v(1.5, 1.5) * mm});
            skLineSegment(sketch, "E201", {"start": v(1.5, 1.5) * mm, "end": v(4, 1.5) * mm});
            skLineSegment(sketch, "E202", {"start": v(4, 1.5) * mm, "end": v(4, -1) * mm});
            skSolve(sketch);
        }
        {
            var Q0;
            {var subQ27=sQuery(id+"F27.wireOp",EDGE,"E179");Q0=makeQuery(id+"F27.imprint","IMPRINT",FACE,{"disambiguationData":[TD([[makeQuery(id+"F27.imprint","IMPRINT",EDGE,{"derivedFrom":subQ27}),-1.0]])]});}
            var Q1;
            {var subQ0=sQuery(id+"F27.wireOp",EDGE,"E194");Q1=makeQuery(id+"F27.imprint","IMPRINT",FACE,{"disambiguationData":[TD([[makeQuery(id+"F27.imprint","IMPRINT",EDGE,{"derivedFrom":subQ0}),1.0]])]});}
            extrude(context, id + "F28", {"entities" : qUnion([Q0, Q1]), "operationType" : NewBodyOperationType.ADD, "depth" : 1 * mm, "offsetDistance" : 25 * mm});
        }
    });
